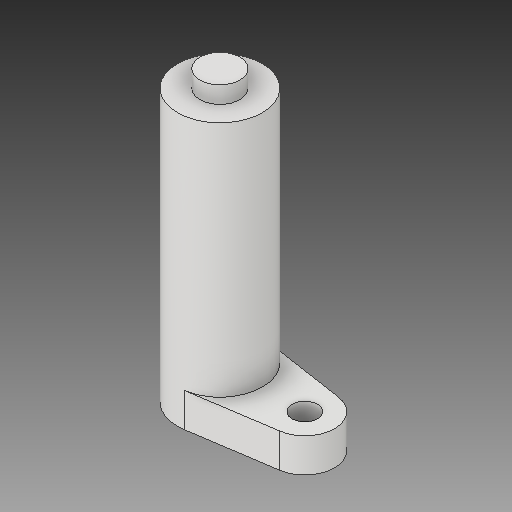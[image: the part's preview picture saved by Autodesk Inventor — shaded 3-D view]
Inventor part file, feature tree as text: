
AUTODESK INVENTOR PART (.ipt)
format: ipt  version: 2018.2 (Build 222227000, 227)  size: 138,752 bytes
history: native  units: mm
features: extrude x4, sketch x3, plane x2, hole x1, fillet x1, projected_geometry x1
ambient origin geometry x8: Origin, YZ Plane, XZ Plane, XY Plane, X Axis, Y Axis, Z Axis, Center Point
bodies: Solid1 (feature_tree)
feature tree (12):
  sketch  "Sketch1"  dims[d0=4.7mm d1=10.0mm]
  extrude  "Extrusion1"  Depth=10.0mm
  extrude  "Extrusion2"  Depth=10.0mm
  extrude  "Extrusion3"  Depth=2.0mm TaperAngle=0.0deg
  plane  "Work Plane1"
  plane  "Work Plane2"
  extrude  "Extrusion4"  Depth=30.0mm TaperAngle=0.0deg
  hole  "Hole1"  [1 undecoded]
  fillet  "Fillet1"  Radius=30.0mm
  sketch  "Sketch2"  dims[d2=3.0mm d3=10.0mm]
  projected_geometry  "Projected Loop1"
  sketch  "Sketch3"  dims[d4=2.0mm d5=2.0mm d6=0.0mm d7=30.0mm d8=0.0mm d9=32.0mm d10=0.0mm d11=30.0mm d12=15.0mm d13=4.0mm d14=0.0mm d17=3.0mm d18=6.0mm d19=4.0mm d20=2.0mm d21=90.0deg d22=8.0mm d23=20.594885mm d24=20.0mm d25=20.0mm d26=-7.0mm d27=2.0mm d28=2.0mm d29=0.0mm]
note: 1 required parameter value undecoded (feature->parameter linkage not recoverable at this tier; creation-order binding heuristic only, values carry confidence <= 0.55)
